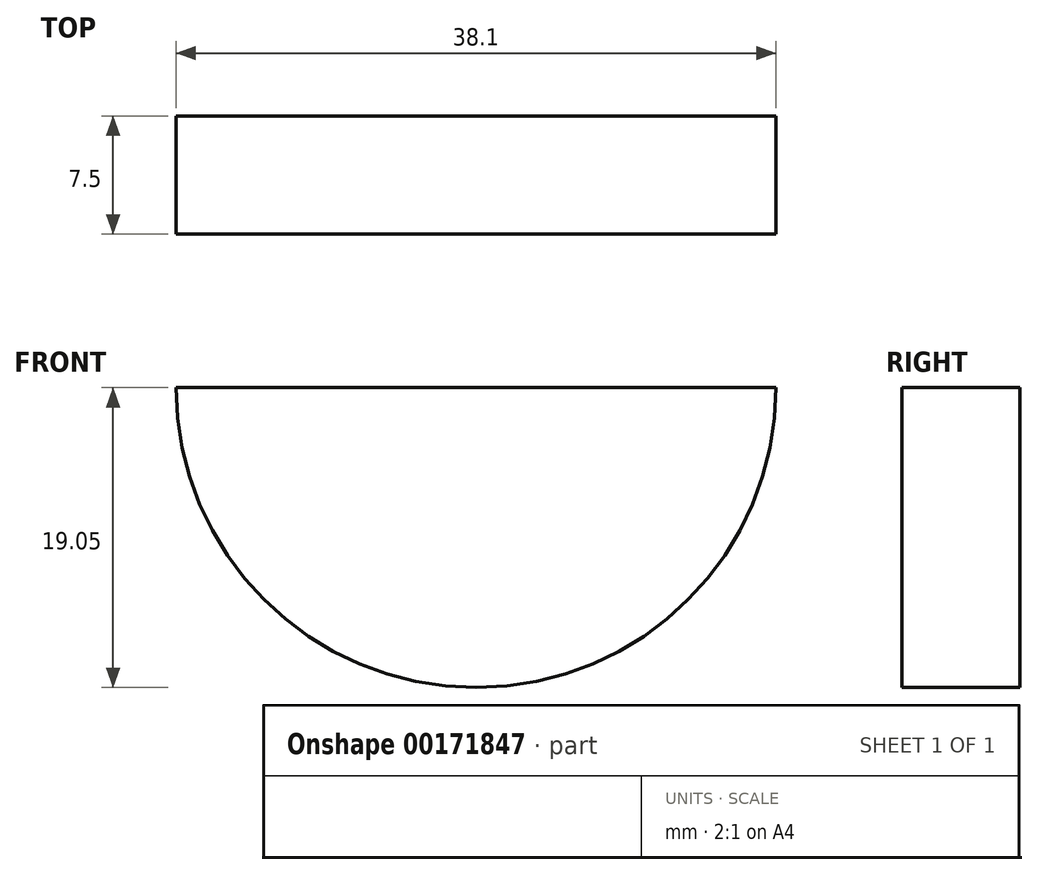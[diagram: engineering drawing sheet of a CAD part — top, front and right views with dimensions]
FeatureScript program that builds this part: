
annotation { "Feature Type Name" : "Feature", "Feature Type Description" : "" }
export const myFeature = defineFeature(function(context is Context, id is Id, definition is map)
    precondition{}
    {
        {
            var Q0;
            Q0=qCreatedBy(makeId("Front.planeOp"),FACE);
            var sketch = newSketch(context, id + "F0", { "sketchPlane" : qUnion([Q0])});
            skCircle(sketch, "E0", {"center": v(-35.76, 8.5) * mm, "radius": 19.05 * mm});
            skLineSegment(sketch, "E1", {"start": v(-54.8, 8.5) * mm, "end": v(-16.7, 8.5) * mm});
            skSolve(sketch);
        }
        {
            var Q0;
            {var subQ0=sQuery(id+"F0.wireOp",EDGE,"E1");Q0=makeQuery(id+"F0.imprint","IMPRINT",FACE,{"disambiguationData":[TD([[makeQuery(id+"F0.imprint","IMPRINT",EDGE,{"derivedFrom":subQ0}),-1.0]])]});}
            extrude(context, id + "F1", {"entities" : qUnion([Q0]), "depth" : 7.5 * mm});
        }
    });
